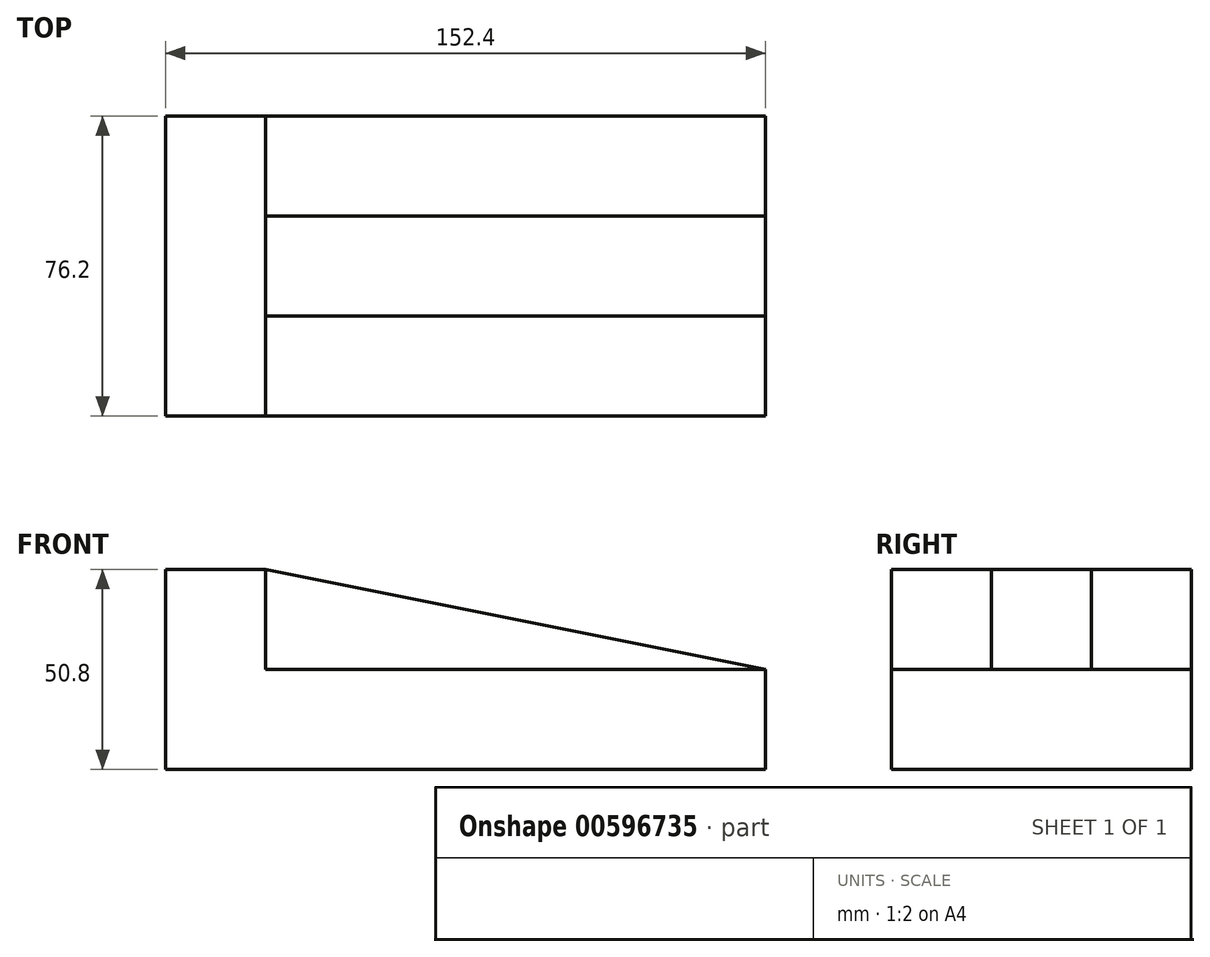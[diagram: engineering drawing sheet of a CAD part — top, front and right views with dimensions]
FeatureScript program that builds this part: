
annotation { "Feature Type Name" : "Feature", "Feature Type Description" : "" }
export const myFeature = defineFeature(function(context is Context, id is Id, definition is map)
    precondition{}
    {
        {
            var Q0;
            Q0=qCreatedBy(makeId("Front.planeOp"),FACE);
            var sketch = newSketch(context, id + "F0", { "sketchPlane" : qUnion([Q0])});
            skLineSegment(sketch, "E0.bottom", {"start": v(0, 0) * mm, "end": v(152.4, 0) * mm});
            skLineSegment(sketch, "E0.top", {"start": v(0, 25.4) * mm, "end": v(152.4, 25.4) * mm});
            skLineSegment(sketch, "E0.left", {"start": v(0, 0) * mm, "end": v(0, 25.4) * mm});
            skLineSegment(sketch, "E0.right", {"start": v(152.4, 0) * mm, "end": v(152.4, 25.4) * mm});
            skSolve(sketch);
        }
        {
            var Q0;
            Q0=makeQuery(id+"F0.imprint","IMPRINT",FACE,{"disambiguationData":[TD([[makeQuery(id+"F0.imprint","IMPRINT",EDGE,{"derivedFrom":sQuery(id+"F0.wireOp",EDGE,"E0.bottom")}),1.0]])]});
            extrude(context, id + "F1", {"entities" : qUnion([Q0]), "depth" : 76.2 * mm, "offsetDistance" : 25.4 * mm});
        }
        {
            var Q0;
            Q0=makeQuery(id+"F1.opExtrude","CAP_FACE",FACE,{"disambiguationData":[OSD([sQuery(id+"F0.wireOp",EDGE,"E0.bottom"),sQuery(id+"F0.wireOp",EDGE,"E0.top"),sQuery(id+"F0.wireOp",EDGE,"E0.left"),sQuery(id+"F0.wireOp",EDGE,"E0.right")])],"isStart":false});
            var sketch = newSketch(context, id + "F2", { "sketchPlane" : qUnion([Q0])});
            skLineSegment(sketch, "E1.0.0", {"start": v(152.4, 25.4) * mm, "end": v(0, 25.4) * mm});
            skLineSegment(sketch, "E1.0.1", {"start": v(0, 25.4) * mm, "end": v(0, 0) * mm});
            skLineSegment(sketch, "E1.0.2", {"start": v(0, 0) * mm, "end": v(152.4, 0) * mm});
            skLineSegment(sketch, "E1.0.3", {"start": v(152.4, 0) * mm, "end": v(152.4, 25.4) * mm});
            skLineSegment(sketch, "E2", {"start": v(0, 0) * mm, "end": v(0, 50.8) * mm});
            skLineSegment(sketch, "E3", {"start": v(0, 50.8) * mm, "end": v(25.4, 50.8) * mm});
            skLineSegment(sketch, "E4", {"start": v(25.4, 50.8) * mm, "end": v(25.4, 0) * mm});
            skSolve(sketch);
        }
        {
            var Q0;
            {var subQ5=sQuery(id+"F2.wireOp",EDGE,"E3");Q0=makeQuery(id+"F2.imprint","IMPRINT",FACE,{"disambiguationData":[TD([[makeQuery(id+"F2.imprint","IMPRINT",EDGE,{"derivedFrom":subQ5}),-1.0]])]});}
            extrude(context, id + "F3", {"entities" : qUnion([Q0]), "operationType" : NewBodyOperationType.ADD, "oppositeDirection" : true, "depth" : 76.2 * mm, "offsetDistance" : 25.4 * mm});
        }
        {
            var Q0;
            Q0=makeQuery(id+"F3.opExtrude","SWEPT_FACE",FACE,{"disambiguationData":[OSD([sQuery(id+"F2.wireOp",EDGE,"E4")])]});
            var sketch = newSketch(context, id + "F4", { "sketchPlane" : qUnion([Q0])});
            skLineSegment(sketch, "E5.0.0", {"start": v(-76.2, 50.8) * mm, "end": v(-76.2, 25.4) * mm});
            skLineSegment(sketch, "E5.0.1", {"start": v(-76.2, 25.4) * mm, "end": v(0, 25.4) * mm});
            skLineSegment(sketch, "E5.0.2", {"start": v(0, 25.4) * mm, "end": v(0, 50.8) * mm});
            skLineSegment(sketch, "E5.0.3", {"start": v(0, 50.8) * mm, "end": v(-76.2, 50.8) * mm});
            skLineSegment(sketch, "E6", {"start": v(-76.2, 25.4) * mm, "end": v(-50.8, 25.4) * mm});
            skLineSegment(sketch, "E7", {"start": v(-50.8, 25.4) * mm, "end": v(-50.8, 50.8) * mm});
            skLineSegment(sketch, "E8", {"start": v(-50.8, 50.8) * mm, "end": v(-25.4, 50.8) * mm});
            skLineSegment(sketch, "E9", {"start": v(-25.4, 50.8) * mm, "end": v(-25.4, 25.4) * mm});
            skLineSegment(sketch, "E10", {"start": v(-25.4, 25.4) * mm, "end": v(-50.8, 25.4) * mm});
            skSolve(sketch);
        }
        {
            var Q0;
            Q0=makeQuery(id+"F4.imprint","IMPRINT",FACE,{"disambiguationData":[TD([[makeQuery(id+"F4.imprint","IMPRINT",EDGE,{"derivedFrom":sQuery(id+"F4.wireOp",EDGE,"E7")}),-1.0]])]});
            extrude(context, id + "F5", {"entities" : qUnion([Q0]), "operationType" : NewBodyOperationType.ADD, "depth" : 127 * mm, "offsetDistance" : 25.4 * mm});
        }
        {
            var Q0;
            Q0=makeQuery(id+"F5.opExtrude","SWEPT_FACE",FACE,{"disambiguationData":[OSD([sQuery(id+"F4.wireOp",EDGE,"E7")])]});
            var sketch = newSketch(context, id + "F6", { "sketchPlane" : qUnion([Q0])});
            skLineSegment(sketch, "E11.0.0", {"start": v(25.4, 50.8) * mm, "end": v(25.4, 25.4) * mm});
            skLineSegment(sketch, "E11.0.1", {"start": v(25.4, 25.4) * mm, "end": v(152.4, 25.4) * mm});
            skLineSegment(sketch, "E11.0.2", {"start": v(152.4, 25.4) * mm, "end": v(152.4, 50.8) * mm});
            skLineSegment(sketch, "E11.0.3", {"start": v(152.4, 50.8) * mm, "end": v(25.4, 50.8) * mm});
            skLineSegment(sketch, "E12", {"start": v(25.4, 50.8) * mm, "end": v(152.4, 25.4) * mm});
            skSolve(sketch);
        }
        {
            var Q0;
            Q0=makeQuery(id+"F6.imprint","IMPRINT",FACE,{"disambiguationData":[TD([[makeQuery(id+"F6.imprint","IMPRINT",EDGE,{"derivedFrom":sQuery(id+"F6.wireOp",EDGE,"E11.0.2")}),1.0]])]});
            extrude(context, id + "F7", {"entities" : qUnion([Q0]), "operationType" : NewBodyOperationType.REMOVE, "oppositeDirection" : true, "depth" : 38.6 * mm, "offsetDistance" : 25.4 * mm});
        }
    });
